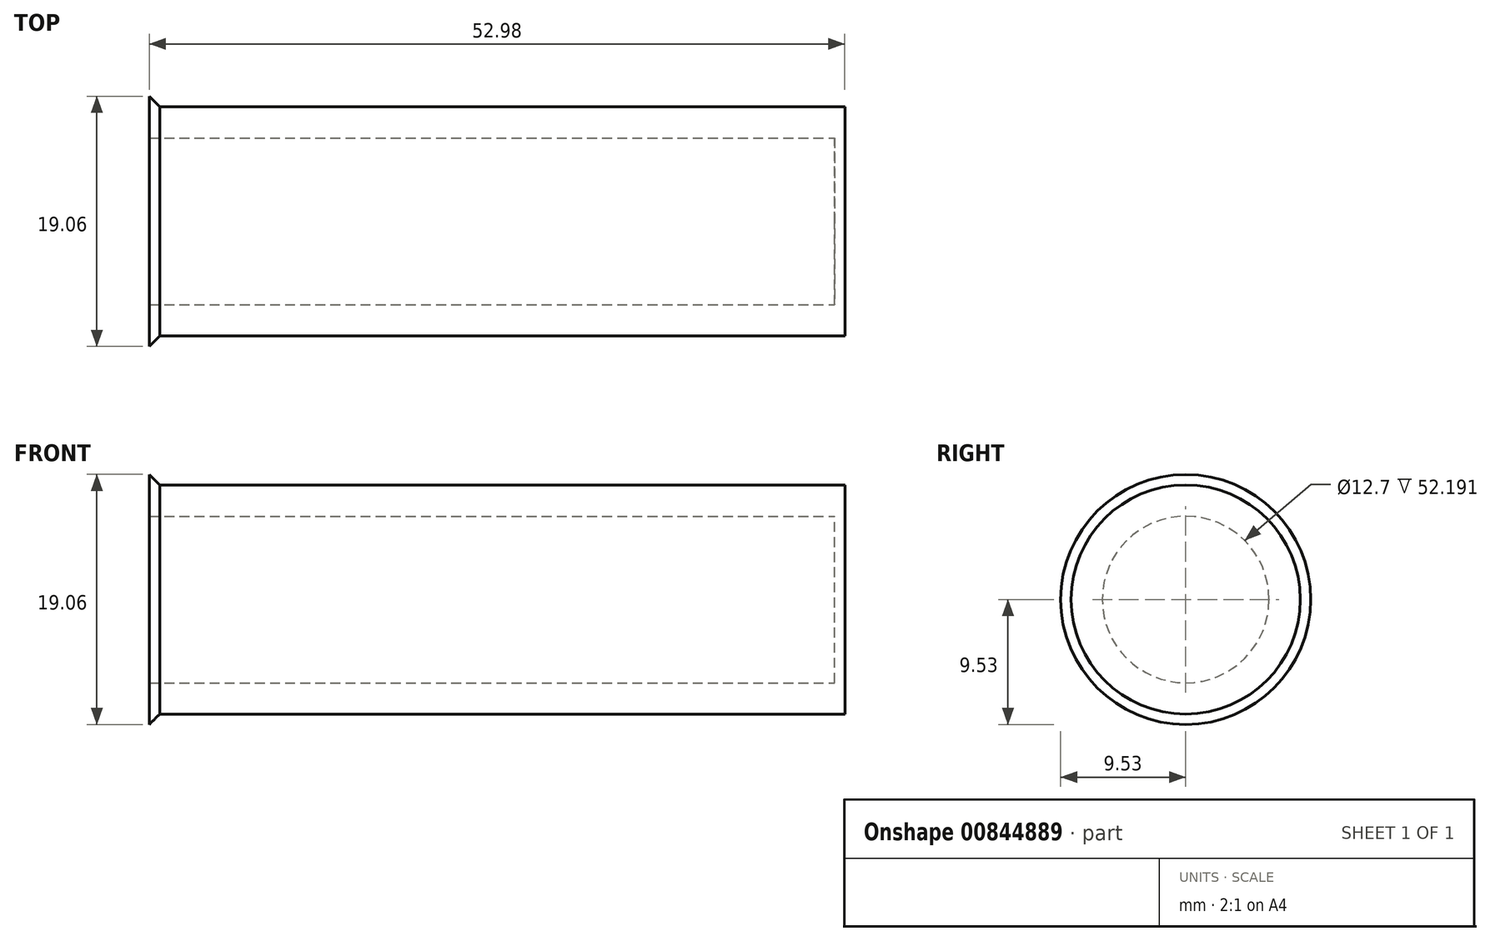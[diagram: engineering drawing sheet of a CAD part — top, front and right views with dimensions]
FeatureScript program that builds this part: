
annotation { "Feature Type Name" : "Feature", "Feature Type Description" : "" }
export const myFeature = defineFeature(function(context is Context, id is Id, definition is map)
    precondition{}
    {
        {
            var Q0;
            Q0=qCreatedBy(makeId("Front.planeOp"),FACE);
            var sketch = newSketch(context, id + "F0", { "sketchPlane" : qUnion([Q0])});
            skLineSegment(sketch, "E0", {"start": v(0, 0) * mm, "end": v(0, 9.53) * mm});
            skLineSegment(sketch, "E1", {"start": v(52.98, 8.73) * mm, "end": v(52.98, 0) * mm});
            skLineSegment(sketch, "E2", {"start": v(52.98, 0) * mm, "end": v(0, 0) * mm, "construction": true});
            skLineSegment(sketch, "E3", {"start": v(0, 9.53) * mm, "end": v(0.8, 8.73) * mm});
            skLineSegment(sketch, "E4", {"start": v(0.8, 8.73) * mm, "end": v(52.98, 8.73) * mm});
            skLineSegment(sketch, "E5", {"start": v(52.2, 6.35) * mm, "end": v(0, 6.35) * mm});
            skLineSegment(sketch, "E6", {"start": v(52.2, 6.35) * mm, "end": v(52.2, 0) * mm});
            skLineSegment(sketch, "E7", {"start": v(52.2, 0) * mm, "end": v(52.98, 0) * mm});
            skSolve(sketch);
        }
        {
            var Q0;
            Q0=makeQuery(id+"F0.imprint","IMPRINT",FACE,{"disambiguationData":[TD([[makeQuery(id+"F0.imprint","IMPRINT",EDGE,{"derivedFrom":sQuery(id+"F0.wireOp",EDGE,"E1")}),-1.0]])]});
            var Q1;
            Q1=sQuery(id+"F0.wireOp",EDGE,"E2");
            revolve(context, id + "F1", {"surfaceOperationType" : NewSurfaceOperationType.NEW, "entities" : qUnion([Q0]), "axis" : qUnion([Q1]), "revolveType" : RevolveType.FULL});
        }
    });
